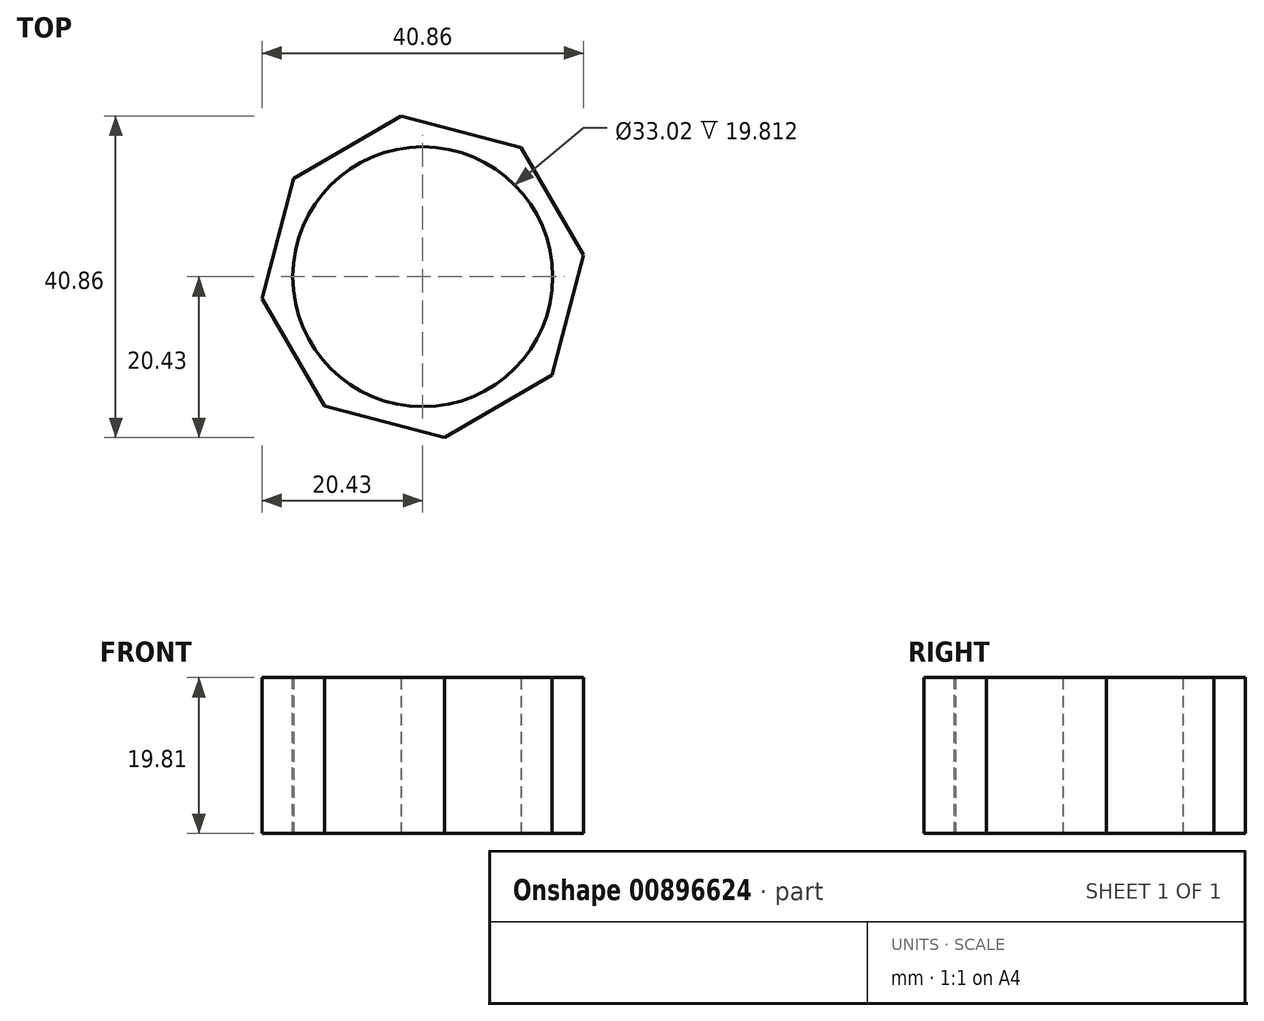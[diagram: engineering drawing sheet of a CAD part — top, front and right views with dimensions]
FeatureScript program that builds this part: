
annotation { "Feature Type Name" : "Feature", "Feature Type Description" : "" }
export const myFeature = defineFeature(function(context is Context, id is Id, definition is map)
    precondition{}
    {
        {
            var Q0;
            Q0=qCreatedBy(makeId("Top.planeOp"),FACE);
            var sketch = newSketch(context, id + "F0", { "sketchPlane" : qUnion([Q0])});
            skCircle(sketch, "E0.cCircle", {"center": v(0, 0) * mm, "radius": 19.05 * mm, "construction": true});
            skLineSegment(sketch, "E0.0", {"start": v(12.49, 16.4) * mm, "end": v(20.43, 2.77) * mm});
            skLineSegment(sketch, "E0.1", {"start": v(20.43, 2.77) * mm, "end": v(16.4, -12.49) * mm});
            skLineSegment(sketch, "E0.2", {"start": v(16.4, -12.49) * mm, "end": v(2.77, -20.43) * mm});
            skLineSegment(sketch, "E0.3", {"start": v(2.77, -20.43) * mm, "end": v(-12.49, -16.4) * mm});
            skLineSegment(sketch, "E0.4", {"start": v(-12.49, -16.4) * mm, "end": v(-20.43, -2.77) * mm});
            skLineSegment(sketch, "E0.5", {"start": v(-20.43, -2.77) * mm, "end": v(-16.4, 12.49) * mm});
            skLineSegment(sketch, "E0.6", {"start": v(-16.4, 12.49) * mm, "end": v(-2.77, 20.43) * mm});
            skLineSegment(sketch, "E0.7", {"start": v(-2.77, 20.43) * mm, "end": v(12.49, 16.4) * mm});
            skPoint(sketch, "E0.0.midPoint", {"position": v(16.46, 9.6) * mm});
            skSolve(sketch);
        }
        {
            var Q0;
            Q0 = qSketchRegion(id + "F0", true);
            extrude(context, id + "F1", {"entities" : qUnion([Q0]), "depth" : 19.8 * mm, "offsetDistance" : 25.4 * mm});
        }
        {
            var Q0;
            Q0=makeQuery(id+"F1.opExtrude","CAP_FACE",FACE,{"disambiguationData":[OSD([sQuery(id+"F0.wireOp",EDGE,"E0.0"),sQuery(id+"F0.wireOp",EDGE,"E0.1"),sQuery(id+"F0.wireOp",EDGE,"E0.2"),sQuery(id+"F0.wireOp",EDGE,"E0.3"),sQuery(id+"F0.wireOp",EDGE,"E0.4"),sQuery(id+"F0.wireOp",EDGE,"E0.5"),sQuery(id+"F0.wireOp",EDGE,"E0.6"),sQuery(id+"F0.wireOp",EDGE,"E0.7")])],"isStart":false});
            var sketch = newSketch(context, id + "F2", { "sketchPlane" : qUnion([Q0])});
            skCircle(sketch, "E1", {"center": v(0, 0) * mm, "radius": 16.51 * mm});
            skSolve(sketch);
        }
        {
            var Q0;
            Q0 = qSketchRegion(id + "F2", true);
            extrude(context, id + "F3", {"entities" : qUnion([Q0]), "operationType" : NewBodyOperationType.REMOVE, "oppositeDirection" : true, "depth" : 25.4 * mm, "offsetDistance" : 25.4 * mm});
        }
    });
